# Revit family: npaa - Door - Single Flush_Fixed2014
name_source: partatom
category: Doors
revit_build: Autodesk Revit 2014 (Build: 20131024_2115(x64)
units: mm (PartAtom-declared; Revit-internal decimal feet)

## types (9) — shared parameters
Analytic Construction = <None>
Function = Interior
Thickness = 51 mm  [stored 0.167323 ft]
Trim Projection Ext = 25 mm  [stored 0.082021 ft]
Trim Projection Int = 25 mm  [stored 0.082021 ft]
Trim Width = 76 mm  [stored 0.249344 ft]
Wall Closure = By host

## per-type parameters (varying)
| type | Door Material | Frame Material | Handle Height | Height | Width |
| 0915 x 2134mm | Door - Panel | Door - Frame | 1035.74 mm | 2134 mm  [stored 7.00131 ft] | 915 mm  [stored 3.00197 ft] |
| 0864 x 2134mm | Door - Panel | Door - Frame | 1035.74 mm | 2134 mm  [stored 7.00131 ft] | 864 mm |
| 0813 x 2134mm | Door - Panel | Door - Frame | 1035.74 mm | 2134 mm  [stored 7.00131 ft] | 813 mm  [stored 2.66732 ft] |
| 0762 x 2134mm | Door - Panel | Door - Frame | 1035.74 mm | 2134 mm  [stored 7.00131 ft] | 762 mm  [stored 2.5 ft] |
| 0762 x 2032mm | Door - Panel | Door - Frame | 1035.74 mm | 2032 mm  [stored 6.66667 ft] | 762 mm  [stored 2.5 ft] |
| 0915 x 2032mm | Door - Panel | Door - Frame | 1035.74 mm | 2032 mm  [stored 6.66667 ft] | 915 mm  [stored 3.00197 ft] |
| 0864 x 2032mm | Door - Panel | Door - Frame | 900 mm  [stored 2.95276 ft] | 2032 mm  [stored 6.66667 ft] | 864 mm |
| 0915 x 2032mm 2 | Door - Panel 2 | Door - Frame 2 | 1035.74 mm | 2032 mm  [stored 6.66667 ft] | 915 mm  [stored 3.00197 ft] |
| 2700 x 2700 | Door - Panel | Door - Frame | 1035.74 mm | 2700 mm  [stored 8.85827 ft] | 2700 mm  [stored 8.85827 ft] |

note: [stored X ft] marks values corroborated as IEEE doubles in the binary element streams (Revit-internal decimal feet)

## geometry (parser evidence)
native form markers: Sweep x2
no freeform markers — native parametric forms only
